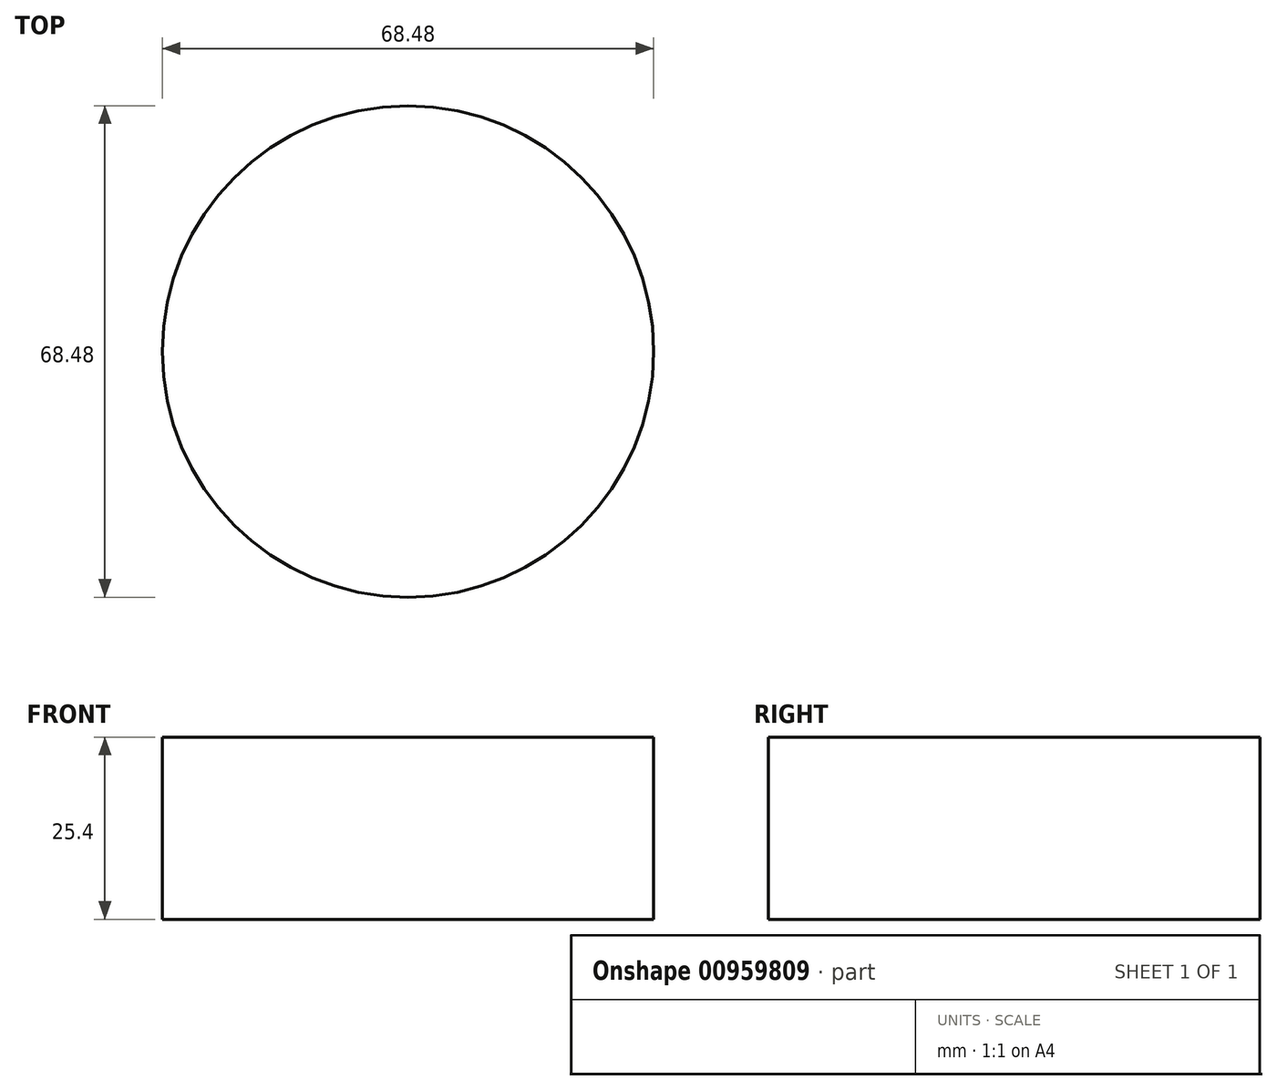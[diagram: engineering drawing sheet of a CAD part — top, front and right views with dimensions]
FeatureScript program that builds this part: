
annotation { "Feature Type Name" : "Feature", "Feature Type Description" : "" }
export const myFeature = defineFeature(function(context is Context, id is Id, definition is map)
    precondition{}
    {
        {
            var Q0;
            Q0=qCreatedBy(makeId("Top.planeOp"),FACE);
            var sketch = newSketch(context, id + "F0", { "sketchPlane" : qUnion([Q0])});
            skCircle(sketch, "E0", {"center": v(0, 0) * mm, "radius": 34.24 * mm});
            skSolve(sketch);
        }
        {
            var Q0;
            Q0=makeQuery(id+"F0.imprint","IMPRINT",FACE,{"disambiguationData":[TD([[makeQuery(id+"F0.imprint","IMPRINT",EDGE,{"derivedFrom":sQuery(id+"F0.wireOp",EDGE,"E0")}),1.0]])]});
            extrude(context, id + "F1", {"entities" : qUnion([Q0]), "depth" : 25.4 * mm, "offsetDistance" : 25.4 * mm});
        }
    });
